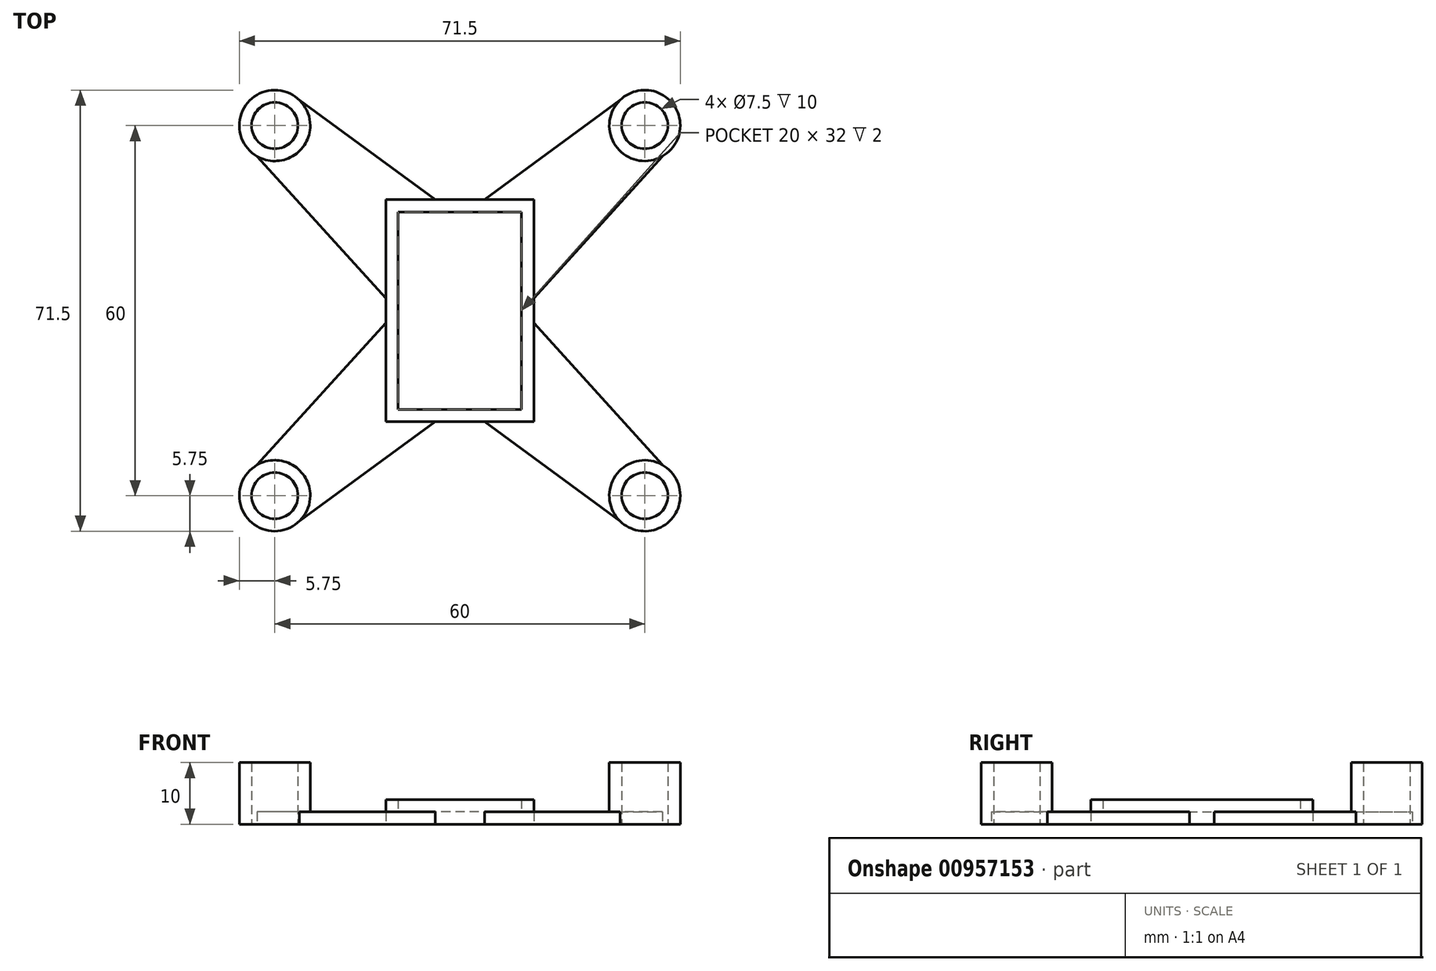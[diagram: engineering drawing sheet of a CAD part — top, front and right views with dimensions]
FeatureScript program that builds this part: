
annotation { "Feature Type Name" : "Feature", "Feature Type Description" : "" }
export const myFeature = defineFeature(function(context is Context, id is Id, definition is map)
    precondition{}
    {
        {
            var Q0;
            Q0=qCreatedBy(makeId("Top.planeOp"),FACE);
            var sketch = newSketch(context, id + "F0", { "sketchPlane" : qUnion([Q0])});
            skLineSegment(sketch, "E0.bottom", {"start": v(-30, 30) * mm, "end": v(30, 30) * mm, "construction": true});
            skLineSegment(sketch, "E0.top", {"start": v(-30, -30) * mm, "end": v(30, -30) * mm, "construction": true});
            skLineSegment(sketch, "E0.left", {"start": v(-30, 30) * mm, "end": v(-30, -30) * mm, "construction": true});
            skLineSegment(sketch, "E0.right", {"start": v(30, 30) * mm, "end": v(30, -30) * mm, "construction": true});
            skPoint(sketch, "E0.middle", {"position": v(0, 0) * mm});
            skCircle(sketch, "E1", {"center": v(-30, 30) * mm, "radius": 3.75 * mm});
            skCircle(sketch, "E2", {"center": v(30, 30) * mm, "radius": 3.75 * mm});
            skCircle(sketch, "E3", {"center": v(30, -30) * mm, "radius": 3.75 * mm});
            skCircle(sketch, "E4", {"center": v(-30, -30) * mm, "radius": 3.75 * mm});
            skCircle(sketch, "E5", {"center": v(-30, 30) * mm, "radius": 5.75 * mm});
            skCircle(sketch, "E6", {"center": v(30, 30) * mm, "radius": 5.75 * mm});
            skCircle(sketch, "E7", {"center": v(30, -30) * mm, "radius": 5.75 * mm});
            skCircle(sketch, "E8", {"center": v(-30, -30) * mm, "radius": 5.75 * mm});
            skLineSegment(sketch, "E9.bottom", {"start": v(-10, 16) * mm, "end": v(10, 16) * mm});
            skLineSegment(sketch, "E9.top", {"start": v(-10, -16) * mm, "end": v(10, -16) * mm});
            skLineSegment(sketch, "E9.left", {"start": v(-10, 16) * mm, "end": v(-10, -16) * mm});
            skLineSegment(sketch, "E9.right", {"start": v(10, 16) * mm, "end": v(10, -16) * mm});
            skLineSegment(sketch, "E10.bottom", {"start": v(-12, 18) * mm, "end": v(12, 18) * mm});
            skLineSegment(sketch, "E10.top", {"start": v(-12, -18) * mm, "end": v(12, -18) * mm});
            skLineSegment(sketch, "E10.left", {"start": v(-12, 18) * mm, "end": v(-12, -18) * mm});
            skLineSegment(sketch, "E10.right", {"start": v(12, 18) * mm, "end": v(12, -18) * mm});
            skLineSegment(sketch, "E11", {"start": v(-4, 18) * mm, "end": v(-26, 34.13) * mm});
            skLineSegment(sketch, "E12", {"start": v(-12, 2) * mm, "end": v(-32.84, 25) * mm});
            skLineSegment(sketch, "E13.MirrorCS", {"start": v(4, 18) * mm, "end": v(26, 34.13) * mm});
            skLineSegment(sketch, "E14.MirrorCS", {"start": v(12, 2) * mm, "end": v(32.84, 25) * mm});
            skLineSegment(sketch, "E15.MirrorCS", {"start": v(12, -2) * mm, "end": v(32.84, -25) * mm});
            skLineSegment(sketch, "E16.MirrorCS", {"start": v(4, -18) * mm, "end": v(26, -34.13) * mm});
            skLineSegment(sketch, "E17.MirrorCS", {"start": v(-4, -18) * mm, "end": v(-26, -34.13) * mm});
            skLineSegment(sketch, "E18.MirrorCS", {"start": v(-12, -2) * mm, "end": v(-32.84, -25) * mm});
            skSolve(sketch);
        }
        {
            var Q0;
            {var subQ0=sQuery(id+"F0.wireOp",EDGE,"E15.MirrorCS");Q0=makeQuery(id+"F0.imprint","IMPRINT",FACE,{"disambiguationData":[TD([[makeQuery(id+"F0.imprint","IMPRINT",EDGE,{"derivedFrom":subQ0}),-1.0]])]});}
            var Q1;
            Q1=makeQuery(id+"F0.imprint","IMPRINT",FACE,{"disambiguationData":[TD([[makeQuery(id+"F0.imprint","IMPRINT",EDGE,{"derivedFrom":sQuery(id+"F0.wireOp",EDGE,"E3")}),-1.0]])]});
            var Q2;
            {var subQ0=sQuery(id+"F0.wireOp",EDGE,"E17.MirrorCS");Q2=makeQuery(id+"F0.imprint","IMPRINT",FACE,{"disambiguationData":[TD([[makeQuery(id+"F0.imprint","IMPRINT",EDGE,{"derivedFrom":subQ0}),-1.0]])]});}
            var Q3;
            Q3=makeQuery(id+"F0.imprint","IMPRINT",FACE,{"disambiguationData":[TD([[makeQuery(id+"F0.imprint","IMPRINT",EDGE,{"derivedFrom":sQuery(id+"F0.wireOp",EDGE,"E9.bottom")}),-1.0]])]});
            var Q4;
            Q4=makeQuery(id+"F0.imprint","IMPRINT",FACE,{"disambiguationData":[TD([[makeQuery(id+"F0.imprint","IMPRINT",EDGE,{"derivedFrom":sQuery(id+"F0.wireOp",EDGE,"E9.bottom")}),1.0]])]});
            var Q5;
            {var subQ0=sQuery(id+"F0.wireOp",EDGE,"E13.MirrorCS");Q5=makeQuery(id+"F0.imprint","IMPRINT",FACE,{"disambiguationData":[TD([[makeQuery(id+"F0.imprint","IMPRINT",EDGE,{"derivedFrom":subQ0}),-1.0]])]});}
            var Q6;
            Q6=makeQuery(id+"F0.imprint","IMPRINT",FACE,{"disambiguationData":[TD([[makeQuery(id+"F0.imprint","IMPRINT",EDGE,{"derivedFrom":sQuery(id+"F0.wireOp",EDGE,"E2")}),-1.0]])]});
            var Q7;
            {var subQ0=sQuery(id+"F0.wireOp",EDGE,"E11");Q7=makeQuery(id+"F0.imprint","IMPRINT",FACE,{"disambiguationData":[TD([[makeQuery(id+"F0.imprint","IMPRINT",EDGE,{"derivedFrom":subQ0}),1.0]])]});}
            var Q8;
            Q8=makeQuery(id+"F0.imprint","IMPRINT",FACE,{"disambiguationData":[TD([[makeQuery(id+"F0.imprint","IMPRINT",EDGE,{"derivedFrom":sQuery(id+"F0.wireOp",EDGE,"E1")}),-1.0]])]});
            var Q9;
            Q9=makeQuery(id+"F0.imprint","IMPRINT",FACE,{"disambiguationData":[TD([[makeQuery(id+"F0.imprint","IMPRINT",EDGE,{"derivedFrom":sQuery(id+"F0.wireOp",EDGE,"E4")}),-1.0]])]});
            extrude(context, id + "F1", {"entities" : qUnion([Q0, Q1, Q2, Q3, Q4, Q5, Q6, Q7, Q8, Q9]), "depth" : 2 * mm, "offsetDistance" : 25 * mm});
        }
        {
            var Q0;
            Q0=makeQuery(id+"F0.imprint","IMPRINT",FACE,{"disambiguationData":[TD([[makeQuery(id+"F0.imprint","IMPRINT",EDGE,{"derivedFrom":sQuery(id+"F0.wireOp",EDGE,"E1")}),-1.0]])]});
            var Q1;
            Q1=makeQuery(id+"F0.imprint","IMPRINT",FACE,{"disambiguationData":[TD([[makeQuery(id+"F0.imprint","IMPRINT",EDGE,{"derivedFrom":sQuery(id+"F0.wireOp",EDGE,"E3")}),-1.0]])]});
            var Q2;
            Q2=makeQuery(id+"F0.imprint","IMPRINT",FACE,{"disambiguationData":[TD([[makeQuery(id+"F0.imprint","IMPRINT",EDGE,{"derivedFrom":sQuery(id+"F0.wireOp",EDGE,"E4")}),-1.0]])]});
            var Q3;
            Q3=makeQuery(id+"F0.imprint","IMPRINT",FACE,{"disambiguationData":[TD([[makeQuery(id+"F0.imprint","IMPRINT",EDGE,{"derivedFrom":sQuery(id+"F0.wireOp",EDGE,"E2")}),-1.0]])]});
            extrude(context, id + "F2", {"entities" : qUnion([Q0, Q1, Q2, Q3]), "operationType" : NewBodyOperationType.ADD, "depth" : 10 * mm, "offsetDistance" : 25 * mm});
        }
        {
            var Q0;
            Q0=makeQuery(id+"F0.imprint","IMPRINT",FACE,{"disambiguationData":[TD([[makeQuery(id+"F0.imprint","IMPRINT",EDGE,{"derivedFrom":sQuery(id+"F0.wireOp",EDGE,"E9.bottom")}),1.0]])]});
            extrude(context, id + "F3", {"entities" : qUnion([Q0]), "operationType" : NewBodyOperationType.ADD, "depth" : 4 * mm, "offsetDistance" : 25 * mm});
        }
    });
